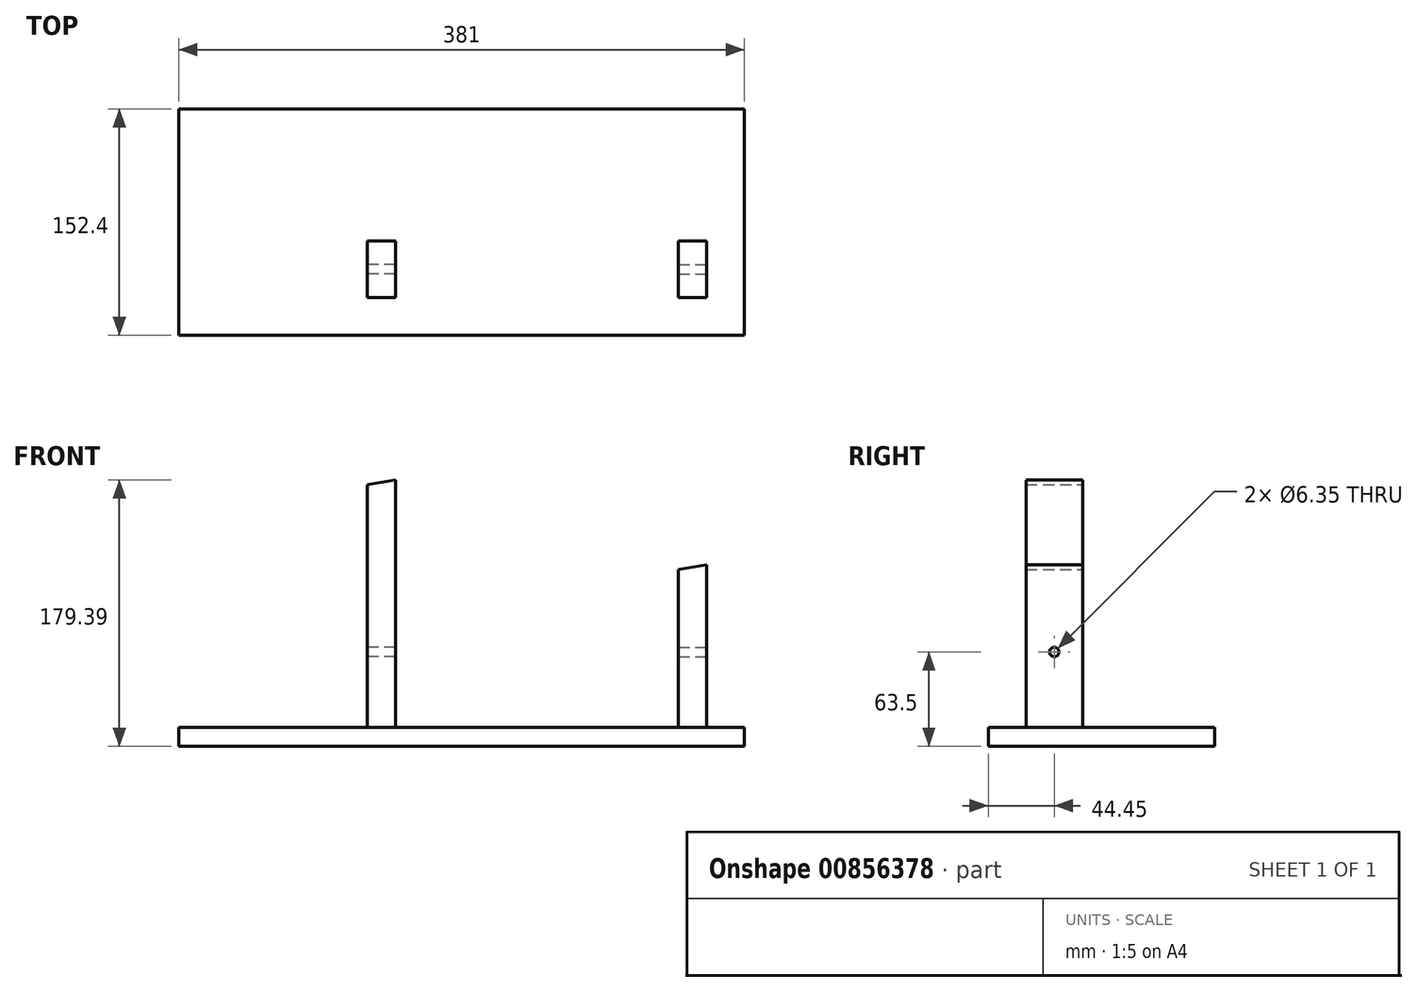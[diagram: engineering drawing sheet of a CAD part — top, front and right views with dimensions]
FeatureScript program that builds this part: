
annotation { "Feature Type Name" : "Feature", "Feature Type Description" : "" }
export const myFeature = defineFeature(function(context is Context, id is Id, definition is map)
    precondition{}
    {
        {
            var Q0;
            Q0=qCreatedBy(makeId("Front.planeOp"),FACE);
            var sketch = newSketch(context, id + "F0", { "sketchPlane" : qUnion([Q0])});
            skLineSegment(sketch, "E0", {"start": v(-208.26, 74.61) * mm, "end": v(207.53, 74.61) * mm, "construction": true});
            skLineSegment(sketch, "E1", {"start": v(-136.11, 65.09) * mm, "end": v(202.37, 65.09) * mm, "construction": true});
            skLineSegment(sketch, "E2", {"start": v(-208.26, 50.8) * mm, "end": v(205.81, 50.8) * mm, "construction": true});
            skLineSegment(sketch, "E3", {"start": v(-208.26, 0) * mm, "end": v(205.81, 0) * mm, "construction": true});
            skLineSegment(sketch, "E4.bottom", {"start": v(79.87, 0) * mm, "end": v(98.92, 0) * mm});
            skLineSegment(sketch, "E4.left", {"start": v(79.87, 0) * mm, "end": v(79.87, 106.36) * mm});
            skLineSegment(sketch, "E4.right", {"start": v(98.92, 0) * mm, "end": v(98.92, 109.54) * mm});
            skLineSegment(sketch, "E5.right", {"start": v(98.92, 109.54) * mm, "end": v(98.92, 109.54) * mm});
            skLineSegment(sketch, "E6", {"start": v(98.92, 109.54) * mm, "end": v(79.87, 106.36) * mm});
            skLineSegment(sketch, "E7", {"start": v(-110.63, 0) * mm, "end": v(-110.63, 166.69) * mm});
            skLineSegment(sketch, "E8", {"start": v(-110.63, 166.69) * mm, "end": v(-129.68, 163.51) * mm});
            skLineSegment(sketch, "E9", {"start": v(-129.68, 163.51) * mm, "end": v(-129.68, 0) * mm});
            skLineSegment(sketch, "E10", {"start": v(-129.68, 0) * mm, "end": v(-110.63, 0) * mm});
            skLineSegment(sketch, "E11.bottom", {"start": v(-256.68, 0) * mm, "end": v(124.32, 0) * mm});
            skLineSegment(sketch, "E11.top", {"start": v(-256.68, -12.7) * mm, "end": v(124.32, -12.7) * mm});
            skLineSegment(sketch, "E11.left", {"start": v(-256.68, 0) * mm, "end": v(-256.68, -12.7) * mm});
            skLineSegment(sketch, "E11.right", {"start": v(124.32, 0) * mm, "end": v(124.32, -12.7) * mm});
            skSolve(sketch);
        }
        {
            var Q0;
            Q0 = qSketchRegion(id + "F0", true);
            extrude(context, id + "F1", {"entities" : qUnion([Q0]), "depth" : 38.1 * mm, "offsetDistance" : 25.4 * mm});
        }
        {
            var Q0;
            Q0=makeQuery(id+"F1.opExtrude","SWEPT_FACE",FACE,{"disambiguationData":[OSD([sQuery(id+"F0.wireOp",EDGE,"E4.right")])]});
            var sketch = newSketch(context, id + "F2", { "sketchPlane" : qUnion([Q0])});
            skCircle(sketch, "E12", {"center": v(-19.05, 50.8) * mm, "radius": 3.18 * mm});
            skPoint(sketch, "E12.first.point", {"position": v(-21.66, 52.61) * mm});
            skPoint(sketch, "E12.second.point", {"position": v(-18.79, 47.64) * mm});
            skPoint(sketch, "E12.third.point", {"position": v(-16.53, 48.86) * mm});
            skSolve(sketch);
        }
        {
            var Q0;
            Q0=makeQuery(id+"F2.imprint","IMPRINT",FACE,{"disambiguationData":[TD([[makeQuery(id+"F2.imprint","IMPRINT",EDGE,{"derivedFrom":sQuery(id+"F2.wireOp",EDGE,"E12")}),1.0]])]});
            var Q1;
            Q1=makeQuery(id+"F1.opExtrude","SWEPT_FACE",FACE,{"disambiguationData":[OSD([sQuery(id+"F0.wireOp",EDGE,"E9")])]});
            extrude(context, id + "F3", {"entities" : qUnion([Q0, Q1]), "operationType" : NewBodyOperationType.REMOVE, "oppositeDirection" : true, "depth" : 19.05 * mm, "offsetDistance" : 25.4 * mm});
        }
        {
            var Q0;
            Q0=makeQuery(id+"F1.opExtrude","SWEPT_FACE",FACE,{"disambiguationData":[OSD([sQuery(id+"F0.wireOp",EDGE,"E9")])]});
            var sketch = newSketch(context, id + "F4", { "sketchPlane" : qUnion([Q0])});
            skCircle(sketch, "E13", {"center": v(19.05, 50.8) * mm, "radius": 3.18 * mm});
            skPoint(sketch, "E13.first.point", {"position": v(17.34, 53.48) * mm});
            skPoint(sketch, "E13.second.point", {"position": v(19.76, 47.7) * mm});
            skPoint(sketch, "E13.third.point", {"position": v(16.4, 49.05) * mm});
            skSolve(sketch);
        }
        {
            var Q0;
            Q0 = qSketchRegion(id + "F4", true);
            extrude(context, id + "F5", {"entities" : qUnion([Q0]), "operationType" : NewBodyOperationType.REMOVE, "oppositeDirection" : true, "depth" : 19.05 * mm, "offsetDistance" : 25.4 * mm});
        }
        {
            var Q0;
            Q0=makeQuery(id+"F1.opExtrude","CAP_FACE",FACE,{"disambiguationData":[OSD([sQuery(id+"F0.wireOp",EDGE,"E4.left"),sQuery(id+"F0.wireOp",EDGE,"E4.right"),sQuery(id+"F0.wireOp",EDGE,"E6"),sQuery(id+"F0.wireOp",EDGE,"E7"),sQuery(id+"F0.wireOp",EDGE,"E8"),sQuery(id+"F0.wireOp",EDGE,"E9"),sQuery(id+"F0.wireOp",EDGE,"E11.bottom"),sQuery(id+"F0.wireOp",EDGE,"E11.top"),sQuery(id+"F0.wireOp",EDGE,"E11.left"),sQuery(id+"F0.wireOp",EDGE,"E11.right")])],"isStart":false});
            var sketch = newSketch(context, id + "F6", { "sketchPlane" : qUnion([Q0])});
            skLineSegment(sketch, "E14", {"start": v(-256.68, 0) * mm, "end": v(124.32, 0) * mm});
            skLineSegment(sketch, "E15", {"start": v(124.32, 0) * mm, "end": v(124.32, -12.7) * mm});
            skLineSegment(sketch, "E16", {"start": v(124.32, -12.7) * mm, "end": v(-256.68, -12.7) * mm});
            skLineSegment(sketch, "E17", {"start": v(-256.68, -12.7) * mm, "end": v(-256.68, 0) * mm});
            skSolve(sketch);
        }
        {
            var Q0;
            {var subQ2=sQuery(id+"F6.wireOp",EDGE,"E15");Q0=makeQuery(id+"F6.imprint","IMPRINT",FACE,{"disambiguationData":[TD([[makeQuery(id+"F6.imprint","IMPRINT",EDGE,{"derivedFrom":subQ2}),-1.0]])]});}
            extrude(context, id + "F7", {"entities" : qUnion([Q0]), "operationType" : NewBodyOperationType.ADD, "depth" : 25.4 * mm, "offsetDistance" : 25.4 * mm});
        }
        {
            var Q0;
            Q0=makeQuery(id+"F1.opExtrude","CAP_FACE",FACE,{"disambiguationData":[OSD([sQuery(id+"F0.wireOp",EDGE,"E4.left"),sQuery(id+"F0.wireOp",EDGE,"E4.right"),sQuery(id+"F0.wireOp",EDGE,"E6"),sQuery(id+"F0.wireOp",EDGE,"E7"),sQuery(id+"F0.wireOp",EDGE,"E8"),sQuery(id+"F0.wireOp",EDGE,"E9"),sQuery(id+"F0.wireOp",EDGE,"E11.bottom"),sQuery(id+"F0.wireOp",EDGE,"E11.top"),sQuery(id+"F0.wireOp",EDGE,"E11.left"),sQuery(id+"F0.wireOp",EDGE,"E11.right")])],"isStart":true});
            var sketch = newSketch(context, id + "F8", { "sketchPlane" : qUnion([Q0])});
            skLineSegment(sketch, "E18", {"start": v(-124.32, 0) * mm, "end": v(256.68, 0) * mm});
            skLineSegment(sketch, "E19", {"start": v(256.68, 0) * mm, "end": v(256.68, -12.7) * mm});
            skLineSegment(sketch, "E20", {"start": v(256.68, -12.7) * mm, "end": v(-124.32, -12.7) * mm});
            skLineSegment(sketch, "E21", {"start": v(-124.32, -12.7) * mm, "end": v(-124.32, 0) * mm});
            skSolve(sketch);
        }
        {
            var Q0;
            {var subQ5=sQuery(id+"F8.wireOp",EDGE,"E19");Q0=makeQuery(id+"F8.imprint","IMPRINT",FACE,{"disambiguationData":[TD([[makeQuery(id+"F8.imprint","IMPRINT",EDGE,{"derivedFrom":subQ5}),-1.0]])]});}
            extrude(context, id + "F9", {"entities" : qUnion([Q0]), "operationType" : NewBodyOperationType.ADD, "depth" : 88.9 * mm, "offsetDistance" : 25.4 * mm});
        }
    });
